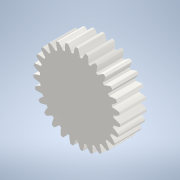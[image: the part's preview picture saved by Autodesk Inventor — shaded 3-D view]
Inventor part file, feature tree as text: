
AUTODESK INVENTOR PART (.ipt)
format: ipt  version: 2022 (Build 260153000, 153)  size: 251,392 bytes
history: native  units: mm (DEFAULTED — no unit token found)
features: plane x3, other x3, sketch x2, extrude x1
ambient origin geometry x8: Origin, YZ Plane, XZ Plane, XY Plane, X Axis, Y Axis, Z Axis, Center Point
bodies: Solid1 (feature_tree)
feature tree (9):
  extrude  "Extrusion1"  Depth=5.0mm TaperAngle=0.0deg
  plane  "Work Plane2"
  plane  "Work Plane8"
  plane  "Work Plane9"
  other  "Spur Gear"
  sketch  "Sketch1"  dims[d0=16.25mm d1=5.0mm d2=0.0mm]
  sketch  "Sketch2"  dims[d3=14.85mm d4=10.0mm d5=0.0mm d16=15.0mm d17=0.0mm d34=1.163553mm d39=0.0mm d41=0.0mm d43=15.0mm d46=15.0mm d47=0.0mm d48=0.0mm d49=6.5mm]
  other  "Srf1"
  other  "Pitch Diameter"
